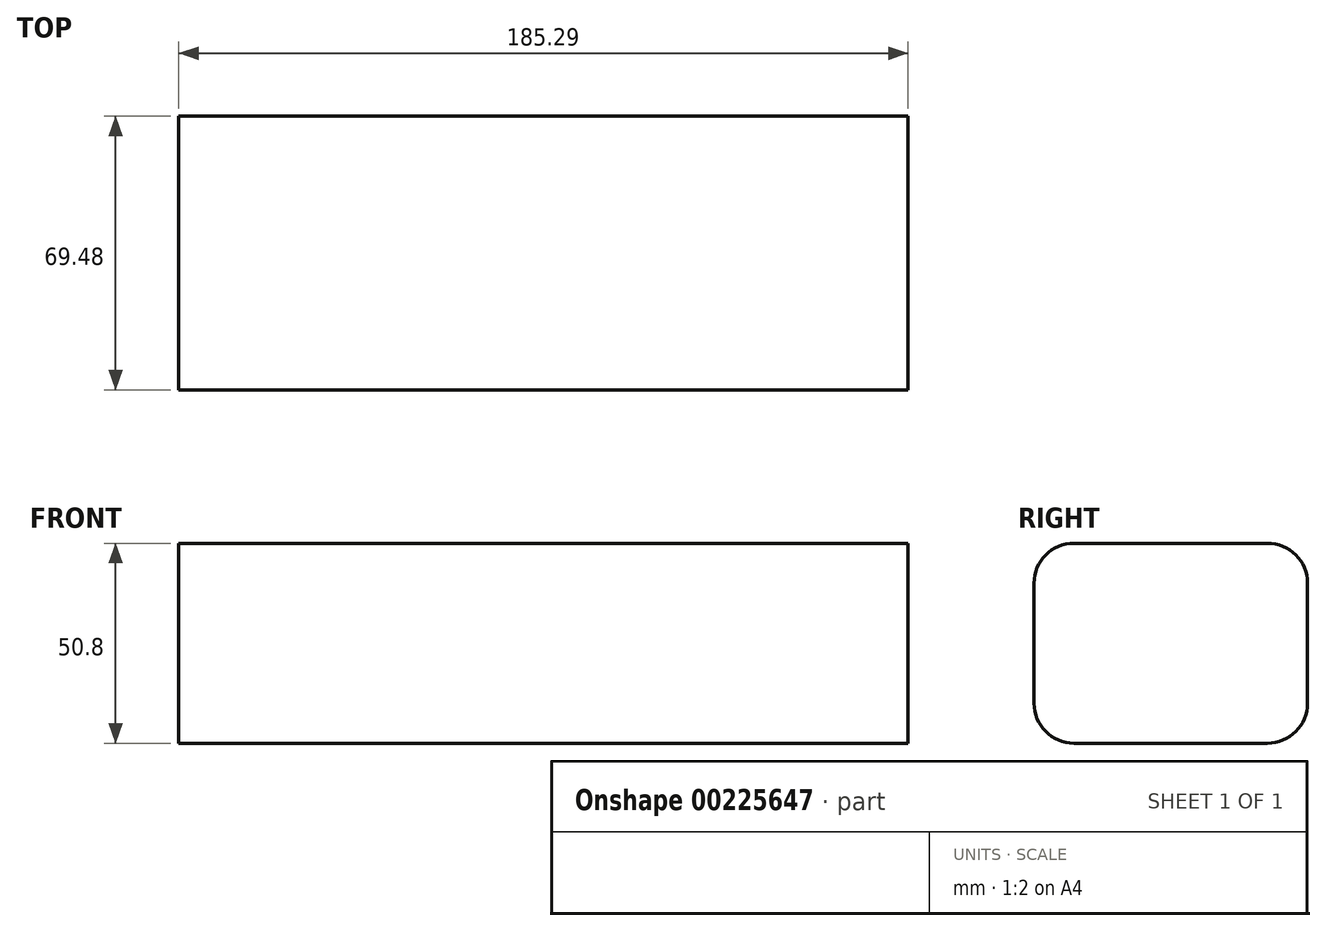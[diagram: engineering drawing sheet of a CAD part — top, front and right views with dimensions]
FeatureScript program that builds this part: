
annotation { "Feature Type Name" : "Feature", "Feature Type Description" : "" }
export const myFeature = defineFeature(function(context is Context, id is Id, definition is map)
    precondition{}
    {
        {
            var Q0;
            Q0=qCreatedBy(makeId("Top.planeOp"),FACE);
            var sketch = newSketch(context, id + "F0", { "sketchPlane" : qUnion([Q0])});
            skLineSegment(sketch, "E0.bottom", {"start": v(-60, 24.56) * mm, "end": v(125.28, 24.56) * mm});
            skLineSegment(sketch, "E0.top", {"start": v(-60, -44.92) * mm, "end": v(125.28, -44.92) * mm});
            skLineSegment(sketch, "E0.left", {"start": v(-60, 24.56) * mm, "end": v(-60, -44.92) * mm});
            skLineSegment(sketch, "E0.right", {"start": v(125.28, 24.56) * mm, "end": v(125.28, -44.92) * mm});
            skSolve(sketch);
        }
        {
            var Q0;
            Q0 = qSketchRegion(id + "F0", true);
            extrude(context, id + "F1", {"entities" : qUnion([Q0]), "endBound" : BoundingType.SYMMETRIC, "depth" : 50.8 * mm});
        }
        {
            var Q0;
            Q0=makeQuery(id+"F1.opExtrude","CAP_EDGE",EDGE,{"disambiguationData":[OSD([sQuery(id+"F0.wireOp",EDGE,"E0.top")])],"isStart":false});
            var Q1;
            Q1=makeQuery(id+"F1.opExtrude","CAP_EDGE",EDGE,{"disambiguationData":[OSD([sQuery(id+"F0.wireOp",EDGE,"E0.bottom")])],"isStart":false});
            var Q2;
            Q2=makeQuery(id+"F1.opExtrude","CAP_EDGE",EDGE,{"disambiguationData":[OSD([sQuery(id+"F0.wireOp",EDGE,"E0.top")])],"isStart":true});
            var Q3;
            Q3=makeQuery(id+"F1.opExtrude","CAP_EDGE",EDGE,{"disambiguationData":[OSD([sQuery(id+"F0.wireOp",EDGE,"E0.bottom")])],"isStart":true});
            fillet(context, id + "F2", {"entities" : qUnion([Q0, Q1, Q2, Q3]), "radius" : 10.16 * mm, "tangentPropagation" : true, "allowEdgeOverflow" : false});
        }
    });
